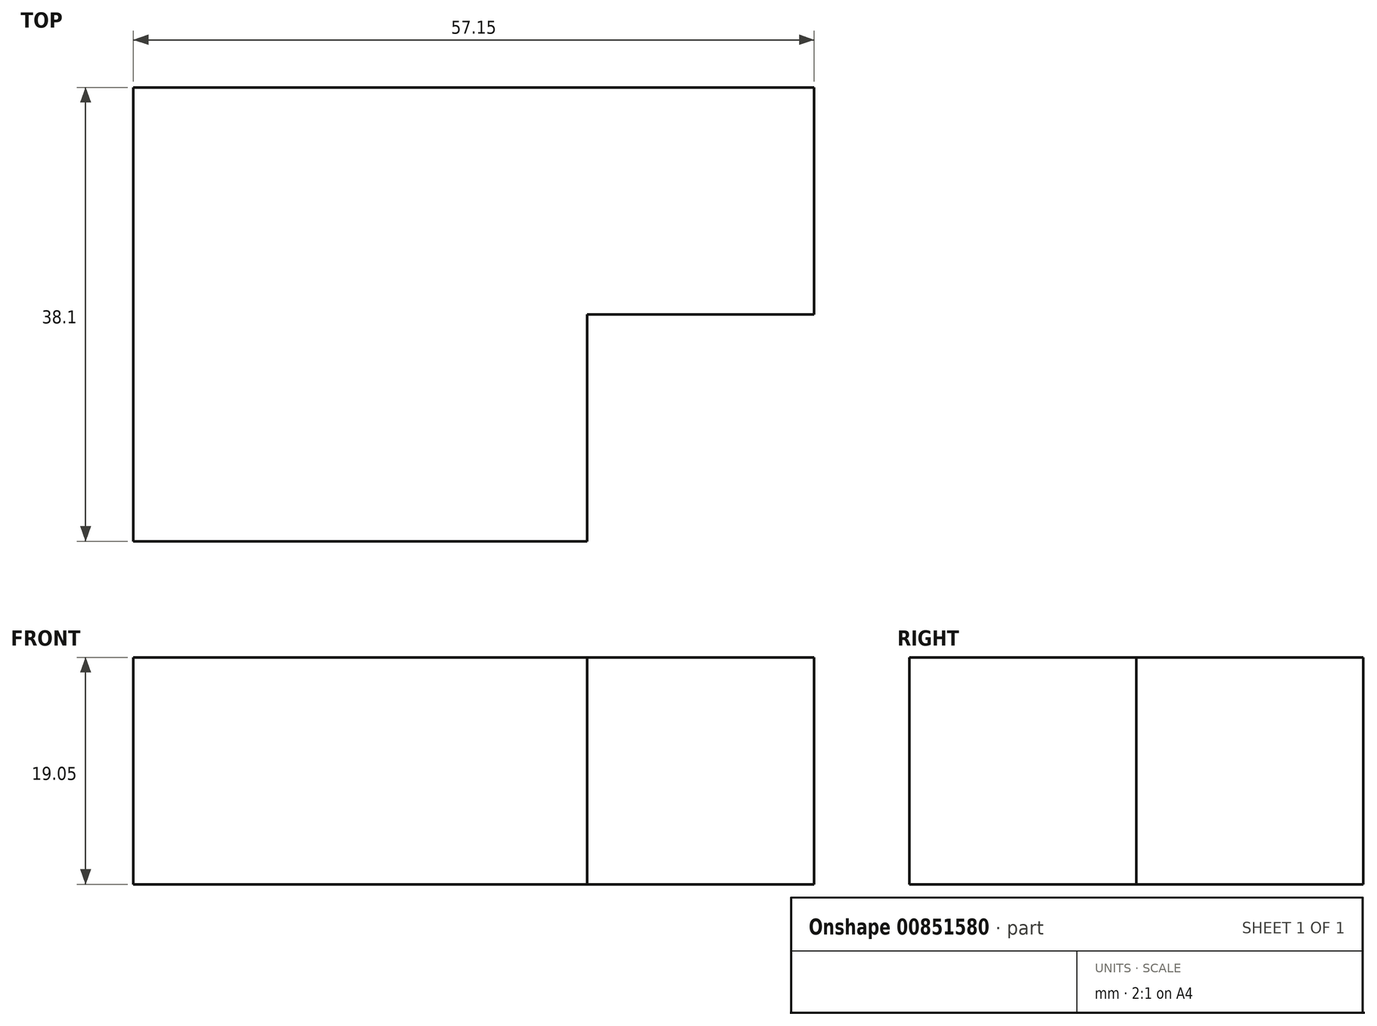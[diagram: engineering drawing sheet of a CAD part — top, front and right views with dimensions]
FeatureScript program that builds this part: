
annotation { "Feature Type Name" : "Feature", "Feature Type Description" : "" }
export const myFeature = defineFeature(function(context is Context, id is Id, definition is map)
    precondition{}
    {
        {
            var Q0;
            Q0=qCreatedBy(makeId("Top.planeOp"),FACE);
            var sketch = newSketch(context, id + "F0", { "sketchPlane" : qUnion([Q0])});
            skLineSegment(sketch, "E0.bottom", {"start": v(19.05, 19.05) * mm, "end": v(-19.05, 19.05) * mm});
            skLineSegment(sketch, "E0.top", {"start": v(19.05, -19.05) * mm, "end": v(-19.05, -19.05) * mm});
            skLineSegment(sketch, "E0.left", {"start": v(19.05, 19.05) * mm, "end": v(19.05, -19.05) * mm});
            skLineSegment(sketch, "E0.right", {"start": v(-19.05, 19.05) * mm, "end": v(-19.05, -19.05) * mm});
            skPoint(sketch, "E0.middle", {"position": v(0, 0) * mm});
            skPoint(sketch, "E1", {"position": v(19.05, 0) * mm});
            skLineSegment(sketch, "E2", {"start": v(19.05, 19.05) * mm, "end": v(38.1, 19.05) * mm});
            skLineSegment(sketch, "E3", {"start": v(38.1, 0) * mm, "end": v(38.1, 19.05) * mm});
            skLineSegment(sketch, "E4", {"start": v(19.05, 0) * mm, "end": v(38.1, 0) * mm});
            skSolve(sketch);
        }
        {
            var Q0;
            {var subQ3=sQuery(id+"F0.wireOp",EDGE,"E0.bottom");Q0=makeQuery(id+"F0.imprint","IMPRINT",FACE,{"disambiguationData":[TD([[makeQuery(id+"F0.imprint","IMPRINT",EDGE,{"derivedFrom":subQ3}),1.0]])]});}
            var Q1;
            {var subQ0=sQuery(id+"F0.wireOp",EDGE,"E2");Q1=makeQuery(id+"F0.imprint","IMPRINT",FACE,{"disambiguationData":[TD([[makeQuery(id+"F0.imprint","IMPRINT",EDGE,{"derivedFrom":subQ0}),-1.0]])]});}
            extrude(context, id + "F1", {"entities" : qUnion([Q0, Q1]), "depth" : 19.05 * mm, "offsetDistance" : 25.4 * mm});
        }
    });
